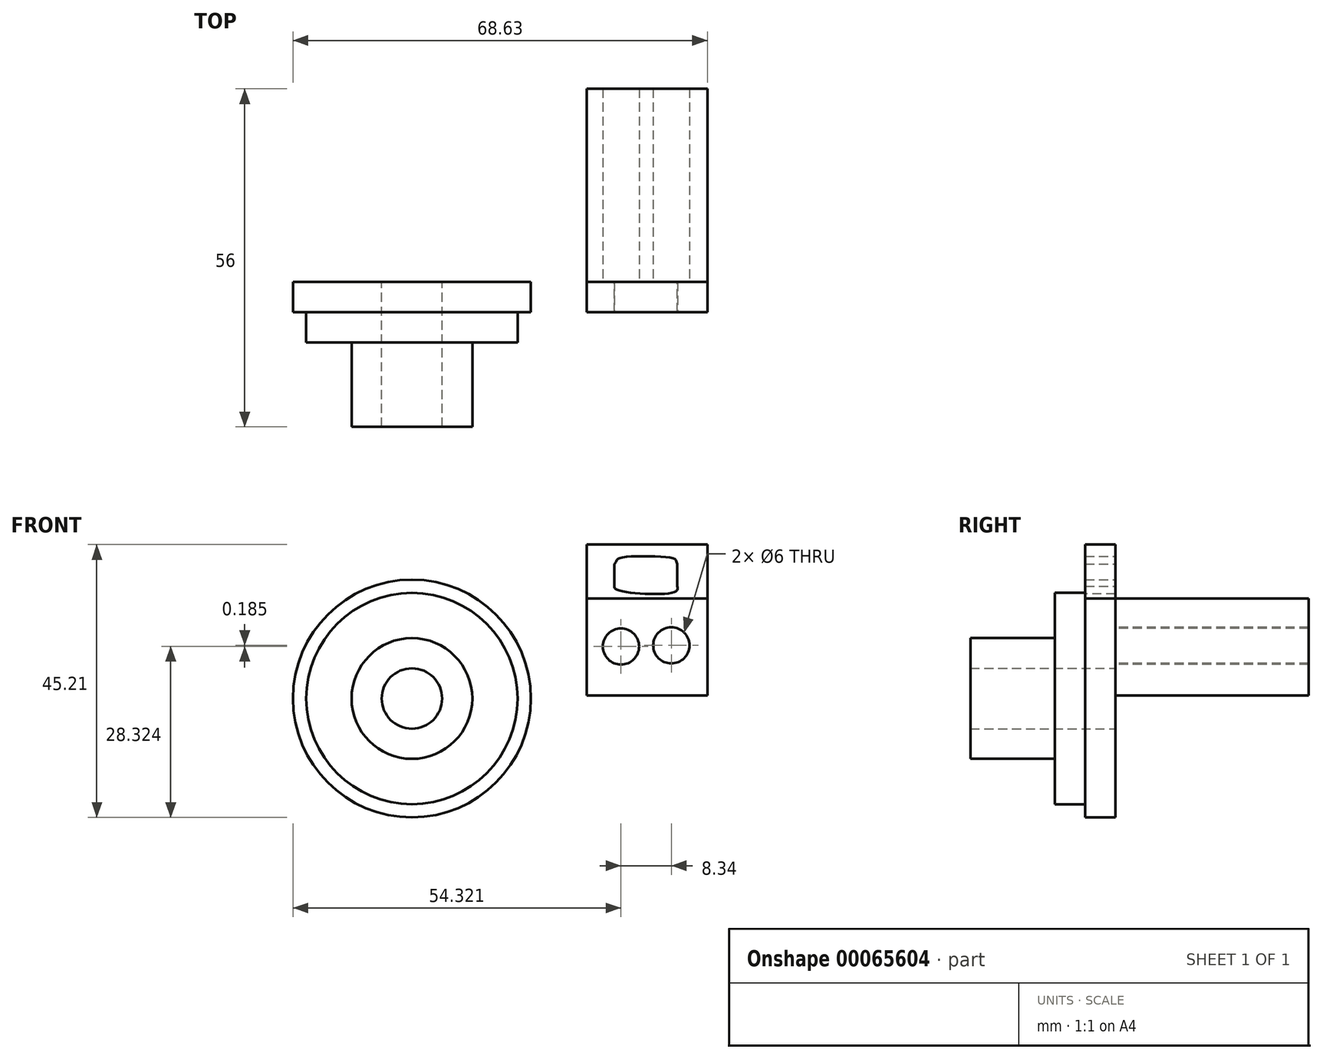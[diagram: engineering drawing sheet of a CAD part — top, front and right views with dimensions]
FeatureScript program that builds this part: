
annotation { "Feature Type Name" : "Feature", "Feature Type Description" : "" }
export const myFeature = defineFeature(function(context is Context, id is Id, definition is map)
    precondition{}
    {
        {
            var Q0;
            Q0=qCreatedBy(makeId("Front.planeOp"),FACE);
            var sketch = newSketch(context, id + "F0", { "sketchPlane" : qUnion([Q0])});
            skCircle(sketch, "E0", {"center": v(0, 0) * mm, "radius": 20 * mm});
            skCircle(sketch, "E1", {"center": v(0, 0) * mm, "radius": 19.7 * mm});
            skCircle(sketch, "E2", {"center": v(0, 0) * mm, "radius": 17.5 * mm});
            skCircle(sketch, "E3", {"center": v(0, 0) * mm, "radius": 10 * mm});
            skCircle(sketch, "E4", {"center": v(0, 0) * mm, "radius": 5 * mm});
            skLineSegment(sketch, "E5", {"start": v(0.42, 0.51) * mm, "end": v(48.93, 0.51) * mm});
            skLineSegment(sketch, "E6", {"start": v(48.93, 0.51) * mm, "end": v(48.93, 25.51) * mm});
            skLineSegment(sketch, "E7", {"start": v(-0.06, 25.5) * mm, "end": v(48.93, 25.51) * mm});
            skLineSegment(sketch, "E8", {"start": v(28.93, 25.51) * mm, "end": v(48.93, 25.51) * mm});
            skLineSegment(sketch, "E9", {"start": v(28.93, 25.51) * mm, "end": v(28.93, 0) * mm});
            skLineSegment(sketch, "E10", {"start": v(28.93, 16.6) * mm, "end": v(48.93, 16.6) * mm});
            skCircle(sketch, "E11", {"center": v(34.62, 8.62) * mm, "radius": 3 * mm});
            skCircle(sketch, "E12", {"center": v(42.96, 8.8) * mm, "radius": 3 * mm});
            skArc(sketch, "E13", {"start": v(-0.06, 25) * mm, "mid": v(-24.06, -6.78) * mm, "end": v(13, -21.36) * mm});
            skLineSegment(sketch, "E14", {"start": v(48.93, 0.51) * mm, "end": v(13, -21.36) * mm});
            skLineSegment(sketch, "E15", {"start": v(-0.06, 25.5) * mm, "end": v(-0.06, 25) * mm});
            skLineSegment(sketch, "E16.trimOffspring", {"start": v(-0.06, 20) * mm, "end": v(-0.06, 19.7) * mm});
            skLineSegment(sketch, "E17", {"start": v(33.54, 22.27) * mm, "end": v(33.54, 18.6) * mm});
            skLineSegment(sketch, "E18", {"start": v(43.95, 22.27) * mm, "end": v(43.95, 18.6) * mm});
            skFitSpline(sketch, "E19", {"points": [v(33.54, 22.27) * mm, v(33.84, 22.69) * mm, v(34.32, 23.23) * mm, v(43.31, 23.22) * mm, v(43.76, 22.83) * mm, v(43.95, 22.27) * mm], "startDerivative": vector(2.96, 3.42) * mm, "endDerivative": vector(1.69, -4.78) * mm});
            skFitSpline(sketch, "E20", {"points": [v(33.54, 18.6) * mm, v(33.92, 18.02) * mm, v(43.62, 17.7) * mm, v(43.95, 18.6) * mm], "startDerivative": vector(-0.04, -3.57) * mm, "endDerivative": vector(-1, 5.1) * mm});
            skSolve(sketch);
        }
        {
            var Q0;
            Q0=makeQuery(id+"F0.imprint","IMPRINT",FACE,{"disambiguationData":[TD([[makeQuery(id+"F0.imprint","IMPRINT",EDGE,{"derivedFrom":sQuery(id+"F0.wireOp",EDGE,"E2")}),-1.0]])]});
            extrude(context, id + "F1", {"entities" : qUnion([Q0]), "depth" : 5 * mm});
        }
        {
            var Q0;
            Q0=makeQuery(id+"F0.imprint","IMPRINT",FACE,{"disambiguationData":[TD([[makeQuery(id+"F0.imprint","IMPRINT",EDGE,{"derivedFrom":sQuery(id+"F0.wireOp",EDGE,"E2")}),1.0]])]});
            extrude(context, id + "F2", {"entities" : qUnion([Q0]), "operationType" : NewBodyOperationType.ADD, "depth" : 10 * mm});
        }
        {
            var Q0;
            Q0=makeQuery(id+"F0.imprint","IMPRINT",FACE,{"disambiguationData":[TD([[makeQuery(id+"F0.imprint","IMPRINT",EDGE,{"derivedFrom":sQuery(id+"F0.wireOp",EDGE,"E3")}),1.0]])]});
            extrude(context, id + "F3", {"entities" : qUnion([Q0]), "operationType" : NewBodyOperationType.ADD, "depth" : 24 * mm});
        }
        {
            var Q0;
            {var subQ0=sQuery(id+"F0.wireOp",EDGE,"E7");Q0=makeQuery(id+"F0.imprint","IMPRINT",FACE,{"disambiguationData":[TD([[makeQuery(id+"F0.imprint","IMPRINT",EDGE,{"derivedFrom":subQ0}),-1.0]])]});}
            extrude(context, id + "F4", {"entities" : qUnion([Q0]), "depth" : 5 * mm});
        }
        {
            var Q0;
            {var subQ0=sQuery(id+"F0.wireOp",EDGE,"E10");Q0=makeQuery(id+"F0.imprint","IMPRINT",FACE,{"disambiguationData":[TD([[makeQuery(id+"F0.imprint","IMPRINT",EDGE,{"derivedFrom":subQ0}),-1.0]])]});}
            var Q1;
            {var subQ2=sQuery(id+"F0.wireOp",EDGE,"E8");Q1=makeQuery(id+"F0.imprint","IMPRINT",FACE,{"disambiguationData":[TD([[makeQuery(id+"F0.imprint","IMPRINT",EDGE,{"derivedFrom":subQ2}),-1.0]])]});}
            extrude(context, id + "F5", {"entities" : qUnion([Q0, Q1]), "operationType" : NewBodyOperationType.ADD, "oppositeDirection" : true, "depth" : 32 * mm});
        }
    });
